# Revit family: Shower-Shower_Door-STERLING-Deluxe-572117
name_source: partatom
category: Specialty Equipment
units: mm (PartAtom-declared; Revit-internal decimal feet)

## family parameters
Cut with Voids When Loaded = No
Host = Face
OmniClass Number = 23.31.17.17
OmniClass Title = Shower Enclosures
Part Type = Normal
Room Calculation Point = No
Round Connector Dimension = Use Diameter
Shared = No

## types (1)
- S-Silver
    ADA Compliant = No
    Assembly Code = C1030200
    Date Modified = 1/11/2023
    Default Elevation = 4"
    Description = Bypass Door 56.25 X 60
    Finish = Sterling-Metal-S-Silver
    Height = 56 1/4"
    Length = 4"
    Manufacturer = Sterling Co.
    Master Format 2014 = 10 28 19.16
    Master Format 2014 Name = Shower Doors
    Material = Premium Metal Construction
    Model = 572117-3G06-S
    Product Documentation Link = https://resources.kohler.com
    Product Name = Deluxe
    Product Page URL = http://www.sterlingplumbing.com
    Type = 1
    URL = https://www.sterlingplumbing.com
    WaterSense Certified = No

## geometry (parser evidence)
native form markers: Sweep x7
no freeform markers — native parametric forms only
